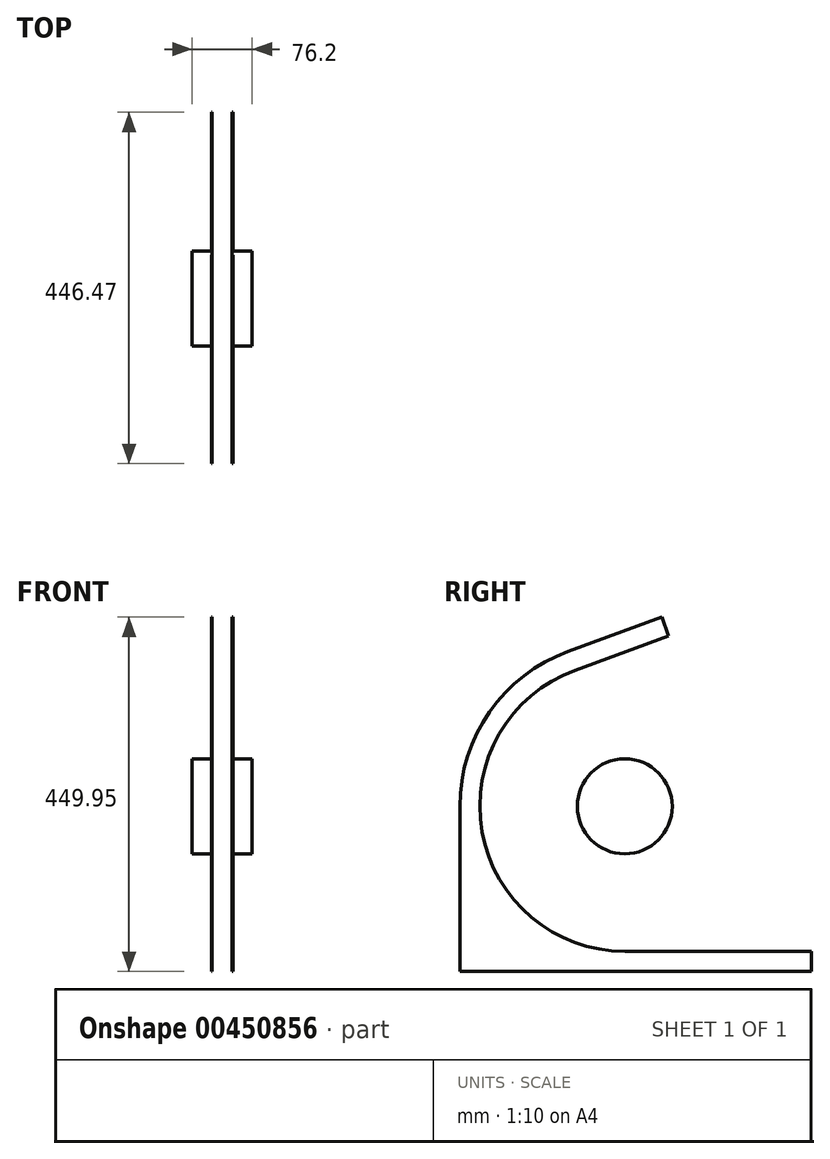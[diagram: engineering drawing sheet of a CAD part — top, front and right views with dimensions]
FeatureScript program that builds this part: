
annotation { "Feature Type Name" : "Feature", "Feature Type Description" : "" }
export const myFeature = defineFeature(function(context is Context, id is Id, definition is map)
    precondition{}
    {
        {
            assignVariable(context, id + "F0", {"name" : "trw", "anyValue" : 1});
        }
        {
            var Q0;
            Q0=qCreatedBy(makeId("Right.planeOp"),FACE);
            var sketch = newSketch(context, id + "F1", { "sketchPlane" : qUnion([Q0])});
            skCircle(sketch, "E0", {"center": v(0, 152.4) * mm, "radius": 60.33 * mm});
            skArc(sketch, "E1", {"start": v(-63.2, 325.37) * mm, "mid": v(-181.33, 120.31) * mm, "end": v(0, -31.75) * mm});
            skArc(sketch, "E2.0", {"start": v(-71.88, 349.23) * mm, "mid": v(-206.35, 115.9) * mm, "end": v(0, -57.15) * mm});
            skLineSegment(sketch, "E3", {"start": v(-71.88, 349.23) * mm, "end": v(-63.2, 325.37) * mm});
            skLineSegment(sketch, "E4", {"start": v(0, -31.75) * mm, "end": v(0, -57.15) * mm});
            skLineSegment(sketch, "E5", {"start": v(0, -31.75) * mm, "end": v(236.92, -31.75) * mm});
            skLineSegment(sketch, "E6", {"start": v(236.92, -31.75) * mm, "end": v(236.92, -57.15) * mm});
            skLineSegment(sketch, "E7", {"start": v(236.92, -57.15) * mm, "end": v(0, -57.15) * mm});
            skLineSegment(sketch, "E8", {"start": v(-63.2, 325.37) * mm, "end": v(55.2, 368.62) * mm});
            skLineSegment(sketch, "E9", {"start": v(-71.88, 349.23) * mm, "end": v(47.4, 392.8) * mm});
            skLineSegment(sketch, "E10", {"start": v(47.4, 392.8) * mm, "end": v(55.2, 368.62) * mm});
            skLineSegment(sketch, "E11", {"start": v(0, 152.4) * mm, "end": v(-363.42, 152.4) * mm, "construction": true});
            skLineSegment(sketch, "E12", {"start": v(0, 152.4) * mm, "end": v(-129.6, 508.5) * mm, "construction": true});
            skLineSegment(sketch, "E13", {"start": v(0, 152.4) * mm, "end": v(0, 16.93) * mm, "construction": true});
            skLineSegment(sketch, "E14", {"start": v(0, 152.4) * mm, "end": v(-390, 294.35) * mm, "construction": true});
            skLineSegment(sketch, "E15", {"start": v(-390, 294.35) * mm, "end": v(0, 152.4) * mm, "construction": true});
            skLineSegment(sketch, "E16", {"start": v(0, 152.4) * mm, "end": v(-348.46, 353.59) * mm, "construction": true});
            skLineSegment(sketch, "E17", {"start": v(0, 152.4) * mm, "end": v(-307.93, 410.78) * mm, "construction": true});
            skLineSegment(sketch, "E18", {"start": v(0, 152.4) * mm, "end": v(-408.92, 224.5) * mm, "construction": true});
            skLineSegment(sketch, "E19", {"start": v(0, 152.4) * mm, "end": v(-391.82, 619.35) * mm, "construction": true});
            skLineSegment(sketch, "E20", {"start": v(0, 152.4) * mm, "end": v(-277.3, 632.7) * mm, "construction": true});
            skLineSegment(sketch, "E21", {"start": v(0, -57.15) * mm, "end": v(-209.55, -57.15) * mm});
            skLineSegment(sketch, "E22", {"start": v(-209.55, -57.15) * mm, "end": v(-209.55, 152.4) * mm});
            skSolve(sketch);
        }
        {
            var Q0;
            Q0=makeQuery(id+"F1.imprint","IMPRINT",FACE,{"disambiguationData":[TD([[makeQuery(id+"F1.imprint","IMPRINT",EDGE,{"derivedFrom":sQuery(id+"F1.wireOp",EDGE,"E0")}),1.0]])]});
            extrude(context, id + "F2", {"entities" : qUnion([Q0]), "depth" : 25.4 * mm});
        }
        {
            var Q0;
            Q0=makeQuery(id+"F1.imprint","IMPRINT",FACE,{"disambiguationData":[TD([[makeQuery(id+"F1.imprint","IMPRINT",EDGE,{"derivedFrom":sQuery(id+"F1.wireOp",EDGE,"E1")}),-1.0]])]});
            var Q1;
            Q1=makeQuery(id+"F1.imprint","IMPRINT",FACE,{"disambiguationData":[TD([[makeQuery(id+"F1.imprint","IMPRINT",EDGE,{"derivedFrom":sQuery(id+"F1.wireOp",EDGE,"E4")}),1.0]])]});
            extrude(context, id + "F3", {"entities" : qUnion([Q0, Q1]), "depth" : (getVariable(context, 'trw')) * mm});
        }
        {
            var Q0;
            Q0=makeQuery(id+"F1.imprint","IMPRINT",FACE,{"disambiguationData":[TD([[makeQuery(id+"F1.imprint","IMPRINT",EDGE,{"derivedFrom":sQuery(id+"F1.wireOp",EDGE,"E3")}),1.0]])]});
            extrude(context, id + "F4", {"entities" : qUnion([Q0]), "operationType" : NewBodyOperationType.ADD, "depth" : (getVariable(context, 'trw')) * mm});
        }
        {
            var Q0;
            {var subQ0=sQuery(id+"F1.wireOp",EDGE,"E21");Q0=makeQuery(id+"F1.imprint","IMPRINT",FACE,{"disambiguationData":[TD([[makeQuery(id+"F1.imprint","IMPRINT",EDGE,{"derivedFrom":subQ0}),-1.0]])]});}
            extrude(context, id + "F5", {"entities" : qUnion([Q0]), "operationType" : NewBodyOperationType.ADD, "depth" : (getVariable(context, 'trw')) * mm});
        }
        {
            var Q0;
            Q0=qCreatedBy(makeId("Right.planeOp"),FACE);
            cPlane(context, id + "F6", {"entities" : qUnion([Q0]), "cplaneType" : CPlaneType.OFFSET, "offset" : 25.4 * mm, "oppositeDirection" : true, "width" : 152.4 * mm, "height" : 152.4 * mm});
        }
        {
            var Q0;
            Q0=qCreatedBy(id+"F6.planeOp",FACE);
            var sketch = newSketch(context, id + "F7", { "sketchPlane" : qUnion([Q0])});
            skCircle(sketch, "E23.0", {"center": v(0, 152.4) * mm, "radius": 60.33 * mm});
            skArc(sketch, "E24.0", {"start": v(-63.2, 325.37) * mm, "mid": v(-181.33, 120.31) * mm, "end": v(0, -31.75) * mm});
            skArc(sketch, "E25.0", {"start": v(-71.88, 349.23) * mm, "mid": v(-206.35, 115.9) * mm, "end": v(0, -57.15) * mm});
            skLineSegment(sketch, "E26.0", {"start": v(-71.88, 349.23) * mm, "end": v(-63.2, 325.37) * mm});
            skLineSegment(sketch, "E27.0", {"start": v(0, -31.75) * mm, "end": v(236.92, -31.75) * mm});
            skLineSegment(sketch, "E28.0", {"start": v(236.92, -57.15) * mm, "end": v(0, -57.15) * mm});
            skLineSegment(sketch, "E29.0", {"start": v(236.92, -31.75) * mm, "end": v(236.92, -57.15) * mm});
            skLineSegment(sketch, "E30.0", {"start": v(-71.88, 349.23) * mm, "end": v(47.4, 392.8) * mm});
            skLineSegment(sketch, "E31.0", {"start": v(-63.2, 325.37) * mm, "end": v(55.2, 368.62) * mm});
            skLineSegment(sketch, "E32.0", {"start": v(47.4, 392.8) * mm, "end": v(55.2, 368.62) * mm});
            skLineSegment(sketch, "E33.0", {"start": v(-209.55, -57.15) * mm, "end": v(-209.55, 152.4) * mm});
            skLineSegment(sketch, "E34.0", {"start": v(236.92, -57.15) * mm, "end": v(-209.55, -57.15) * mm});
            skSolve(sketch);
        }
        {
            var Q0;
            Q0=makeQuery(id+"F7.imprint","IMPRINT",FACE,{"disambiguationData":[TD([[makeQuery(id+"F7.imprint","IMPRINT",EDGE,{"derivedFrom":sQuery(id+"F7.wireOp",EDGE,"E23.0")}),1.0]])]});
            extrude(context, id + "F8", {"entities" : qUnion([Q0]), "operationType" : NewBodyOperationType.ADD, "oppositeDirection" : true, "depth" : 25.4 * mm});
        }
        {
            var Q0;
            Q0=makeQuery(id+"F7.imprint","IMPRINT",FACE,{"disambiguationData":[TD([[makeQuery(id+"F7.imprint","IMPRINT",EDGE,{"derivedFrom":sQuery(id+"F7.wireOp",EDGE,"E24.0")}),-1.0]])]});
            extrude(context, id + "F9", {"entities" : qUnion([Q0]), "oppositeDirection" : true, "depth" : (getVariable(context, 'trw')) * mm});
        }
        {
            var Q0;
            Q0=makeQuery(id+"F7.imprint","IMPRINT",FACE,{"disambiguationData":[TD([[makeQuery(id+"F7.imprint","IMPRINT",EDGE,{"derivedFrom":sQuery(id+"F7.wireOp",EDGE,"E26.0")}),1.0]])]});
            extrude(context, id + "F10", {"entities" : qUnion([Q0]), "operationType" : NewBodyOperationType.ADD, "oppositeDirection" : true, "depth" : (getVariable(context, 'trw')) * mm});
        }
        {
            var Q0;
            {var subQ3=sQuery(id+"F7.wireOp",EDGE,"E33.0");Q0=makeQuery(id+"F7.imprint","IMPRINT",FACE,{"disambiguationData":[TD([[makeQuery(id+"F7.imprint","IMPRINT",EDGE,{"derivedFrom":subQ3}),-1.0]])]});}
            extrude(context, id + "F11", {"entities" : qUnion([Q0]), "operationType" : NewBodyOperationType.ADD, "oppositeDirection" : true, "depth" : (getVariable(context, 'trw')) * mm});
        }
    });
